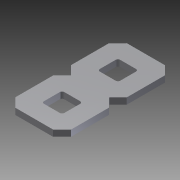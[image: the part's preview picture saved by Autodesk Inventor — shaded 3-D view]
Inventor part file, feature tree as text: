
AUTODESK INVENTOR PART (.ipt)
format: ipt  version: 2014 (Build 180170000, 170)  size: 458,752 bytes
history: native  units: in
note: dims shown in document units (in); Inventor stores cm internally (conversion verified against a paired STEP export)
features: other x1, imported_body x1, extrude x1, sketch x1
ambient origin geometry x8: Origin, YZ Plane, XZ Plane, XY Plane, X Axis, Y Axis, Z Axis, Center Point
bodies: Body1 (feature_tree)
feature tree (4):
  parser-record x1  (decoder bookkeeping rows leaked as tree rows — omitted from the tree; the rows remain in map.json)
  imported_body  "Base1"
  extrude  "Extrusion1"  [1 undecoded]
  sketch  "Sketch1"  dims[d0=1.0in d1=0.0in]
note: 1 required parameter value undecoded (feature->parameter linkage not recoverable at this tier; creation-order binding heuristic only, values carry confidence <= 0.55)
